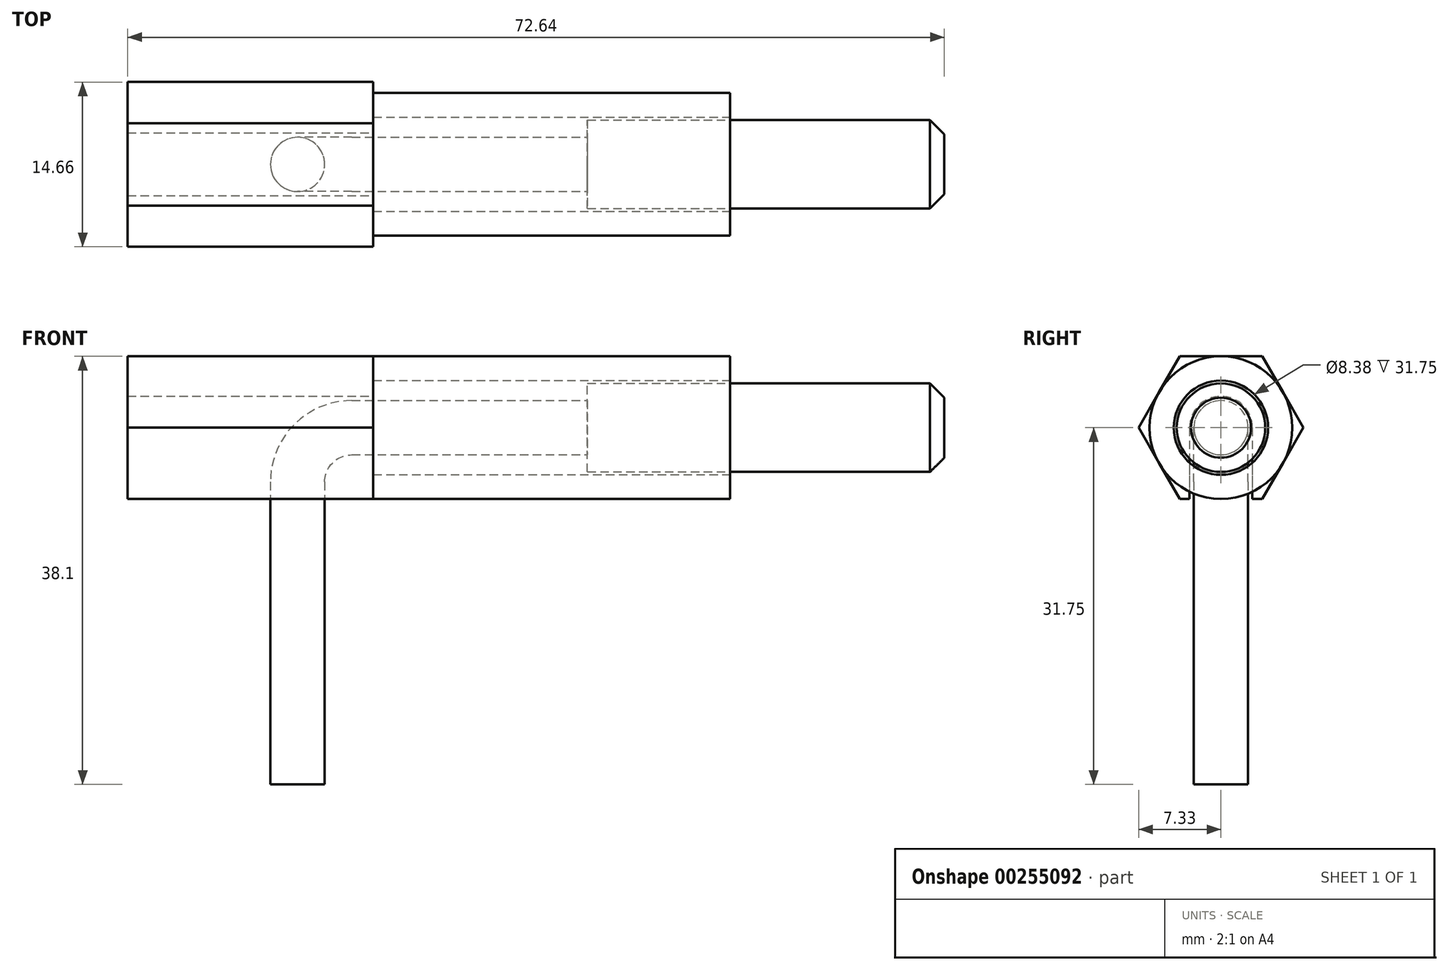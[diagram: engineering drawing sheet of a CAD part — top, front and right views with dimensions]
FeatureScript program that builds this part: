
annotation { "Feature Type Name" : "Feature", "Feature Type Description" : "" }
export const myFeature = defineFeature(function(context is Context, id is Id, definition is map)
    precondition{}
    {
        {
            var Q0;
            Q0=qCreatedBy(makeId("Right.planeOp"),FACE);
            var sketch = newSketch(context, id + "F0", { "sketchPlane" : qUnion([Q0])});
            skCircle(sketch, "E0", {"center": v(0, 0) * mm, "radius": 6.35 * mm});
            skSolve(sketch);
        }
        {
            var Q0;
            Q0 = qSketchRegion(id + "F0", true);
            extrude(context, id + "F1", {"entities" : qUnion([Q0]), "depth" : 31.75 * mm});
        }
        {
            var Q0;
            Q0=makeQuery(id+"F1.opExtrude","CAP_FACE",FACE,{"disambiguationData":[OSD([sQuery(id+"F0.wireOp",EDGE,"E0")])],"isStart":false});
            var sketch = newSketch(context, id + "F2", { "sketchPlane" : qUnion([Q0])});
            skCircle(sketch, "E1", {"center": v(0, 0) * mm, "radius": 4.2 * mm});
            skSolve(sketch);
        }
        {
            var Q0;
            Q0 = qSketchRegion(id + "F2", true);
            extrude(context, id + "F3", {"entities" : qUnion([Q0]), "operationType" : NewBodyOperationType.REMOVE, "endBound" : BoundingType.THROUGH_ALL, "oppositeDirection" : true, "depth" : 19.05 * mm});
        }
        {
            var Q0;
            Q0=makeQuery(id+"F1.opExtrude","CAP_FACE",FACE,{"disambiguationData":[OSD([sQuery(id+"F0.wireOp",EDGE,"E0")])],"isStart":false});
            cPlane(context, id + "F4", {"entities" : qUnion([Q0]), "cplaneType" : CPlaneType.OFFSET, "offset" : 19.05 * mm, "width" : 152.4 * mm, "height" : 152.4 * mm});
        }
        {
            var Q0;
            Q0=qCreatedBy(id+"F4.planeOp",FACE);
            var sketch = newSketch(context, id + "F5", { "sketchPlane" : qUnion([Q0])});
            skCircle(sketch, "E2", {"center": v(0, 0) * mm, "radius": 3.94 * mm});
            skSolve(sketch);
        }
        {
            var Q0;
            Q0 = qSketchRegion(id + "F5", true);
            extrude(context, id + "F6", {"entities" : qUnion([Q0]), "oppositeDirection" : true, "depth" : 31.75 * mm});
        }
        {
            var Q0;
            Q0=qCreatedBy(makeId("Right.planeOp"),FACE);
            var sketch = newSketch(context, id + "F7", { "sketchPlane" : qUnion([Q0])});
            skPoint(sketch, "E3", {"position": v(0, 6.35) * mm});
            skCircle(sketch, "E4.cCircle", {"center": v(0, 0) * mm, "radius": 6.35 * mm, "construction": true});
            skLineSegment(sketch, "E4.0", {"start": v(-3.67, 6.35) * mm, "end": v(3.67, 6.35) * mm});
            skLineSegment(sketch, "E4.1", {"start": v(3.67, 6.35) * mm, "end": v(7.33, 0) * mm});
            skLineSegment(sketch, "E4.2", {"start": v(7.33, 0) * mm, "end": v(3.67, -6.35) * mm});
            skLineSegment(sketch, "E4.3", {"start": v(3.67, -6.35) * mm, "end": v(2.8, -6.35) * mm});
            skLineSegment(sketch, "E4.4", {"start": v(-3.67, -6.35) * mm, "end": v(-7.33, 0) * mm});
            skLineSegment(sketch, "E4.5", {"start": v(-7.33, 0) * mm, "end": v(-3.67, 6.35) * mm});
            skArc(sketch, "E5", {"start": v(2.8, 0) * mm, "mid": v(0, 2.8) * mm, "end": v(-2.8, 0) * mm});
            skLineSegment(sketch, "E6", {"start": v(-2.8, 0) * mm, "end": v(-2.8, -6.35) * mm});
            skLineSegment(sketch, "E7", {"start": v(2.8, 0) * mm, "end": v(2.8, -6.35) * mm});
            skLineSegment(sketch, "E8.trimOffspring", {"start": v(-2.8, -6.35) * mm, "end": v(-3.67, -6.35) * mm});
            skSolve(sketch);
        }
        {
            var Q0;
            Q0 = qSketchRegion(id + "F7", true);
            extrude(context, id + "F8", {"entities" : qUnion([Q0]), "operationType" : NewBodyOperationType.ADD, "oppositeDirection" : true, "depth" : 21.84 * mm});
        }
        {
            var Q0;
            Q0=makeQuery(id+"F6.opExtrude","CAP_FACE",FACE,{"disambiguationData":[OSD([sQuery(id+"F5.wireOp",EDGE,"E2")])],"isStart":false});
            var sketch = newSketch(context, id + "F9", { "sketchPlane" : qUnion([Q0])});
            skCircle(sketch, "E9", {"center": v(0, 0) * mm, "radius": 2.41 * mm});
            skSolve(sketch);
        }
        {
            var Q0;
            Q0 = qSketchRegion(id + "F9", true);
            extrude(context, id + "F10", {"entities" : qUnion([Q0]), "operationType" : NewBodyOperationType.ADD, "depth" : 20.95 * mm});
        }
        {
            var Q0;
            Q0=qCreatedBy(makeId("Front.planeOp"),FACE);
            var sketch = newSketch(context, id + "F11", { "sketchPlane" : qUnion([Q0])});
            skArc(sketch, "E10", {"start": v(-1.9, 0) * mm, "mid": v(-5.32, -1.41) * mm, "end": v(-6.73, -4.83) * mm});
            skLineSegment(sketch, "E11.0", {"start": v(-1.9, -2.41) * mm, "end": v(-1.9, 2.41) * mm, "construction": true});
            skLineSegment(sketch, "E12", {"start": v(-1.9, -4.83) * mm, "end": v(-14.46, -4.83) * mm, "construction": true});
            skLineSegment(sketch, "E13", {"start": v(-6.73, -4.83) * mm, "end": v(-6.73, -31.75) * mm});
            skSolve(sketch);
        }
        {
            var Q0;
            Q0=makeQuery(id+"F10.opExtrude","CAP_FACE",FACE,{"disambiguationData":[OSD([sQuery(id+"F9.wireOp",EDGE,"E9")])],"isStart":false});
            var Q1;
            Q1=sQuery(id+"F11.wireOp",EDGE,"E10");
            var Q2;
            Q2=sQuery(id+"F11.wireOp",EDGE,"E13");
            sweep(context, id + "F12", {"operationType" : NewBodyOperationType.ADD, "profiles" : qUnion([Q0]), "path" : qUnion([Q1, Q2])});
        }
        {
            var Q0;
            Q0=makeQuery(id+"F6.opExtrude","CAP_EDGE",EDGE,{"disambiguationData":[OSD([sQuery(id+"F5.wireOp",EDGE,"E2")])],"isStart":true});
            chamfer(context, id + "F13", {"entities" : qUnion([Q0]), "width" : 1.27 * mm, "tangentPropagation" : true});
        }
    });
